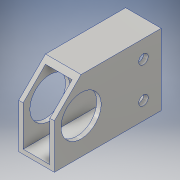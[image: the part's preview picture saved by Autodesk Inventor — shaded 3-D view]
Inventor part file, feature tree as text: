
AUTODESK INVENTOR PART (.ipt)
format: ipt  version: 2016 (Build 200138000, 138)  size: 156,672 bytes
history: native  units: in
note: dims shown in document units (in); Inventor stores cm internally (conversion verified against a paired STEP export)
features: extrude x4, sketch x4
ambient origin geometry x8: Origin, YZ Plane, XZ Plane, XY Plane, X Axis, Y Axis, Z Axis, Center Point
bodies: Solid1 (feature_tree)
feature tree (8):
  extrude  "Extrusion1"  Depth=2.0in
  extrude  "Extrusion2"  Depth=0.125in
  extrude  "Extrusion3"  Depth=0.125in
  extrude  "Extrusion4"  Depth=1.0in
  sketch  "Sketch1"  dims[d0=1.0in d1=2.0in]
  sketch  "Sketch2"  dims[d2=0.125in d3=0.125in]
  sketch  "Sketch3"  dims[d4=0.125in d5=0.125in]
  sketch  "Sketch4"  dims[d6=3.0in d7=0.0in d8=1.125in d9=0.75in d10=1.0in d11=3.0in d12=0.0in d13=135.0deg d14=0.75in d15=3.0in d16=0.0in d17=0.2656in d18=0.5in d19=1.5in d20=0.5in d21=0.5in d22=1.0in d23=0.0in]
